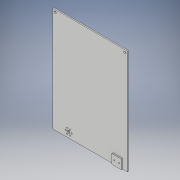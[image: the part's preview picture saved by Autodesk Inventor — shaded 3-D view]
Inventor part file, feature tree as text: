
AUTODESK INVENTOR PART (.ipt)
format: ipt  version: 2017 (Build 210142000, 142)  size: 182,784 bytes
history: native  units: in
note: dims shown in document units (in); Inventor stores cm internally (conversion verified against a paired STEP export)
features: sketch x8, extrude x4, hole x2
ambient origin geometry x8: Origin, YZ Plane, XZ Plane, XY Plane, X Axis, Y Axis, Z Axis, Center Point
bodies: Solid1 (feature_tree)
feature tree (14):
  sketch  "Sketch1"  dims[d0=7.85in d2=0.125in]
  extrude  "Extrusion1"  Depth=0.125in
  extrude  "Extrusion2"  Depth=0.125in
  hole  "Hole1"  [1 undecoded]
  extrude  "Extrusion3"  Depth=0.125in
  sketch  "Sketch6"  dims[d11=4.25in d12=0.125in]
  extrude  "Extrusion4"  Depth=3.6in
  hole  "Hole3"  [1 undecoded]
  sketch  "Sketch2"  dims[d3=0.125in d4=5.674in]
  sketch  "Sketch3"  dims[d5=4.0in d6=0.125in]
  sketch  "Sketch4"  dims[d7=4.0in d8=0.125in]
  sketch  "Sketch5"  dims[d9=1.4in d10=3.6in]
  sketch  "Sketch7"  dims[d13=0.125in]
  sketch  "Sketch9"  dims[d14=0.125in d15=0.0in d16=0.575in d18=1.674in d19=0.0in d20=0.63in d21=0.275in d22=0.125in d23=0.25in d24=0.0in d25=2.3622in d27=360.0deg d29=0.75in d30=0.0in d31=0.5in d32=90.0deg d33=0.5in d34=0.138in d35=0.138in d36=0.104in d37=0.276in d38=0.375in d39=0.25in d40=0.5635in d41=0.432in d42=0.8108in d43=0.25in d44=0.25in d45=1.0in d46=0.125in d47=0.0in d48=0.0in d49=0.5in d50=0.0in d51=0.125in d52=0.0in d64=0.25in d65=0.25in d66=0.25in d67=0.25in d68=0.25in d69=0.75in d70=0.375in d71=0.25in d72=0.5635in d73=0.375in d74=0.8108in]
note: 2 required parameter values undecoded (feature->parameter linkage not recoverable at this tier; creation-order binding heuristic only, values carry confidence <= 0.55)
